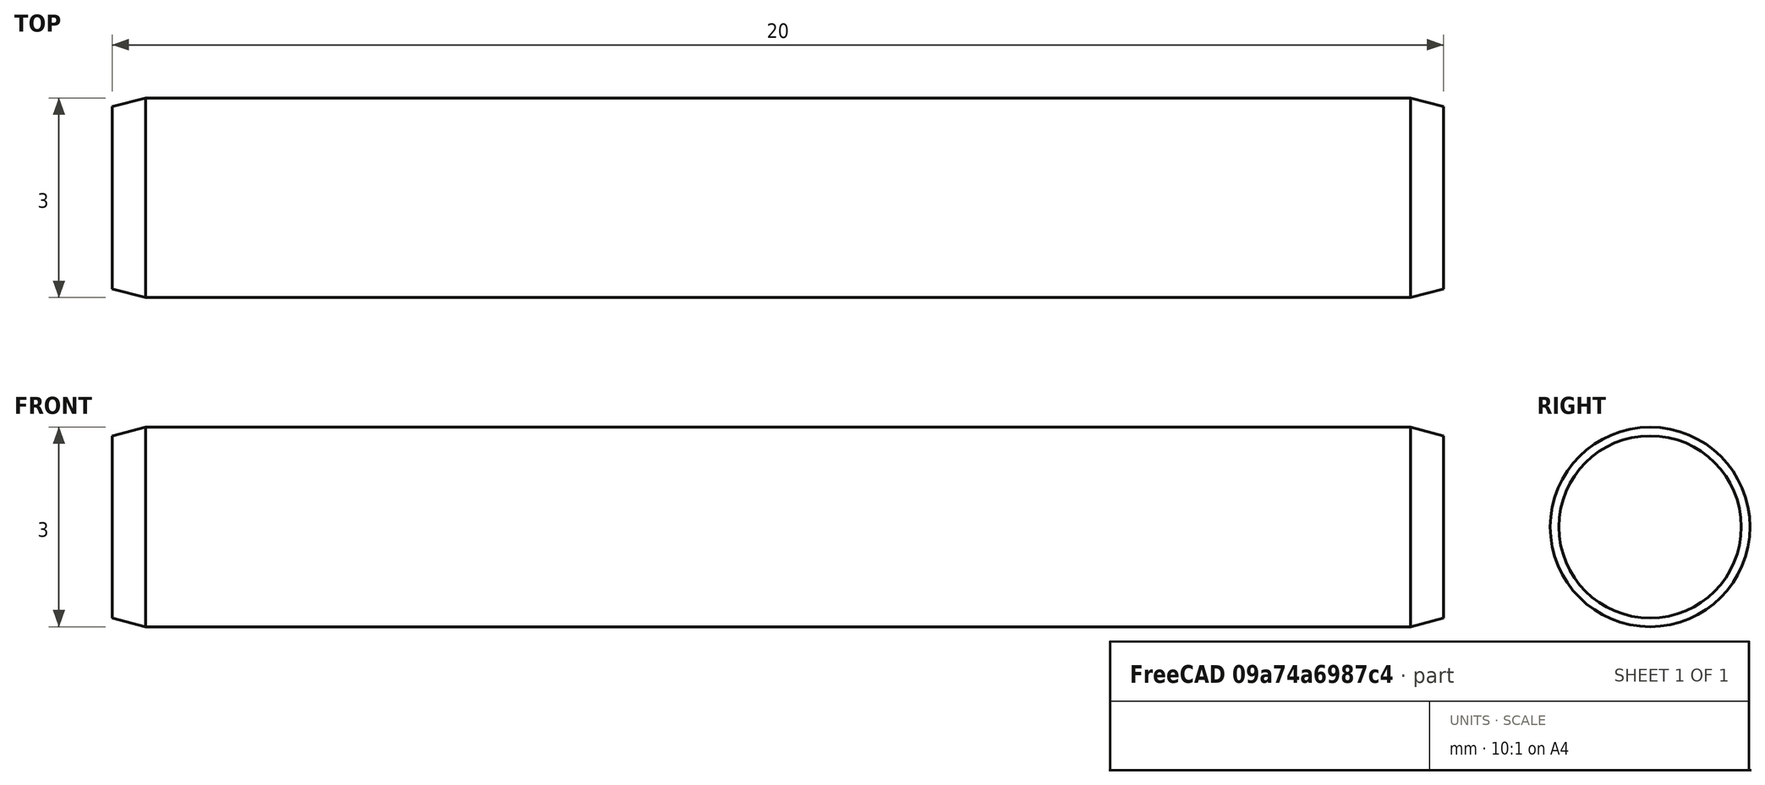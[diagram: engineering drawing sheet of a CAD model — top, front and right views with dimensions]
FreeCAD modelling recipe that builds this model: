
FCSTD DOCUMENT  (FreeCAD 0.14R3702 (Git))
Label: Extruder-lever-pole
License: CC-BY 3.0
LicenseURL: http://creativecommons.org/licenses/by/3.0/
objects: Sketcher::SketchObject×1, PartDesign::Revolution×1, Part::Feature×1
note: 4 computed .brp shape members not serialized (recipe doc carries the construction recipe); baked Part::Feature solids carry a one-line shape summary decoded from their .brp

FEATURE [Sketcher::SketchObject] Sketch
  sketch-geometry (6):
    g0: LineSegment StartX=-10 StartY=0 StartZ=0 EndX=-10 EndY=1.37 EndZ=0
    g1: LineSegment StartX=-10 StartY=1.37 StartZ=0 EndX=-9.5 EndY=1.5 EndZ=0
    g2: LineSegment StartX=-9.5 StartY=1.5 StartZ=0 EndX=9.5 EndY=1.5 EndZ=0
    g3: LineSegment StartX=9.5 StartY=1.5 StartZ=0 EndX=10 EndY=1.37 EndZ=0
    g4: LineSegment StartX=10 StartY=1.37 StartZ=0 EndX=10 EndY=0 EndZ=0
    g5: LineSegment StartX=-10 StartY=0 StartZ=0 EndX=10 EndY=0 EndZ=0
  constraints (18):
    c: Coincident(g0,g1)
    c: Coincident(g1,g2)
    c: Coincident(g2,g3)
    c: Coincident(g3,g4)
    c: Vertical(g0)
    c: Horizontal(g2)
    c: Vertical(g4)
    c: PointOnObject(g0,g-1)
    c: Symmetric(g4,g0,g-2)
    c: Symmetric(g1,g2,g-2)
    c: Horizontal(g5)
    c: Coincident(g5,g0)
    c: Coincident(g5,g4)
    c: DistanceX(g5) = 20
    c: DistanceY(g0,g1) = 1.5
    c: DistanceY(g0) = 1.37
    c: DistanceX(g2) = 19
    c: Symmetric(g0,g3,g-2)
FEATURE [PartDesign::Revolution] Revolution  label="lever-shaft"
  Angle = 360
  Axis = (1,0,0)
  Base = (0,0,0)
  ReferenceAxis = -> Sketch [H_Axis]
  Sketch = -> Sketch
FEATURE [Part::Feature] Revolution001  label="lever-shaft-final"
  shape: bbox 20 x 3 x 3 mm, 5 faces (baked)
